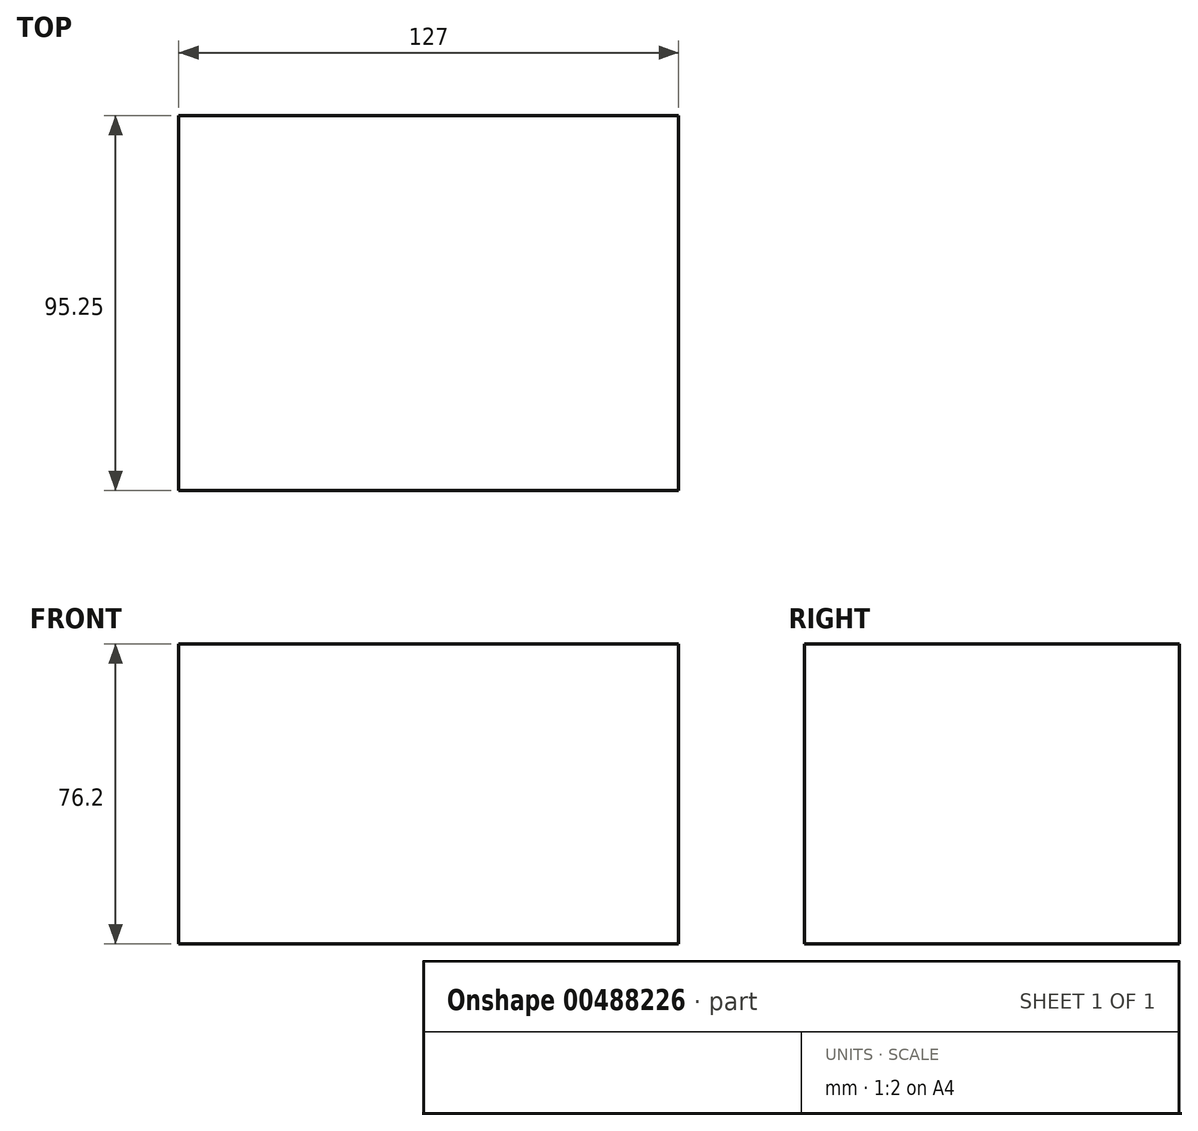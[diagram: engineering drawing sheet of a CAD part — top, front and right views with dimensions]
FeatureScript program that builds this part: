
annotation { "Feature Type Name" : "Feature", "Feature Type Description" : "" }
export const myFeature = defineFeature(function(context is Context, id is Id, definition is map)
    precondition{}
    {
        {
            var Q0;
            Q0=qCreatedBy(makeId("Front.planeOp"),FACE);
            var sketch = newSketch(context, id + "F0", { "sketchPlane" : qUnion([Q0])});
            skLineSegment(sketch, "E0.bottom", {"start": v(63.5, -38.1) * mm, "end": v(-63.5, -38.1) * mm});
            skLineSegment(sketch, "E0.top", {"start": v(63.5, 38.1) * mm, "end": v(-63.5, 38.1) * mm});
            skLineSegment(sketch, "E0.left", {"start": v(63.5, -38.1) * mm, "end": v(63.5, 38.1) * mm});
            skLineSegment(sketch, "E0.right", {"start": v(-63.5, -38.1) * mm, "end": v(-63.5, 38.1) * mm});
            skPoint(sketch, "E0.middle", {"position": v(0, 0) * mm});
            skSolve(sketch);
        }
        {
            var Q0;
            Q0 = qSketchRegion(id + "F0", true);
            extrude(context, id + "F1", {"entities" : qUnion([Q0]), "depth" : 95.25 * mm});
        }
    });
